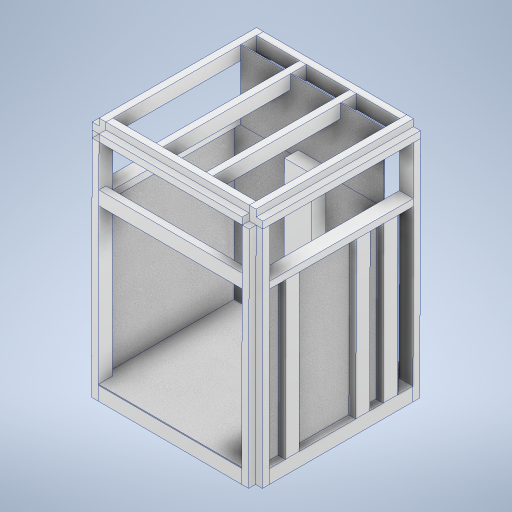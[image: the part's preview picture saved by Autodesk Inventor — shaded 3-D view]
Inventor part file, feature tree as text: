
AUTODESK INVENTOR PART (.ipt)
format: ipt  version: 2024 (Build 280153000, 153)  size: 792,576 bytes
history: native  units: mm
features: projected_geometry x19, extrude x18, sketch x17, mirror x2
ambient origin geometry x8: Origin, YZ Plane, XZ Plane, XY Plane, X Axis, Y Axis, Z Axis, Center Point
bodies: Solid1 (feature_tree), Solid2 (feature_tree), Solid3 (feature_tree), Solid4 (feature_tree), Solid5 (feature_tree), Solid6 (feature_tree), Solid7 (feature_tree), Solid8 (feature_tree), Solid12 (feature_tree), Solid16 (feature_tree), Solid17 (feature_tree), Solid18 (feature_tree), Solid19 (feature_tree), Solid20 (feature_tree), Solid22 (feature_tree), Solid23 (feature_tree), Solid24 (feature_tree), Solid25 (feature_tree)
feature tree (56):
  extrude  "Extrusion1"  Depth=495.0mm
  extrude  "Extrusion2"  Depth=40.0mm
  extrude  "Extrusion3"  Depth=20.0mm
  extrude  "Extrusion4"  Depth=40.0mm
  extrude  "Extrusion5"  Depth=20.0mm
  extrude  "Extrusion6"  Depth=40.0mm
  mirror  "Mirror1"
  extrude  "Extrusion7"  Depth=20.0mm
  extrude  "Extrusion8"  Depth=40.0mm
  extrude  "Extrusion12"  Depth=20.0mm
  mirror  "Mirror2"
  extrude  "Extrusion16"  Depth=40.0mm
  extrude  "Extrusion17"  Depth=20.0mm
  extrude  "Extrusion18"  Depth=40.0mm
  extrude  "Extrusion19"  Depth=20.0mm
  sketch  "Sketch23"  dims[d32=20.0mm d33=20.0mm]
  extrude  "Extrusion23"  Depth=20.0mm TaperAngle=0.0deg
  extrude  "Extrusion24"  Depth=40.0mm
  extrude  "Extrusion25"  Depth=20.0mm
  extrude  "Extrusion20"  Depth=40.0mm
  extrude  "Extrusion22"  Depth=20.0mm
  sketch  "Sketch1"  dims[d0=495.0mm d1=495.0mm]
  sketch  "Sketch2"  dims[d2=40.0mm d3=40.0mm]
  projected_geometry  "Projected Loop1"
  sketch  "Sketch3"  dims[d4=20.0mm d5=20.0mm]
  projected_geometry  "Projected Loop2"
  sketch  "Sketch4"  dims[d6=40.0mm d7=40.0mm]
  projected_geometry  "Projected Loop3"
  projected_geometry  "Projected Loop4"
  sketch  "Sketch5"  dims[d8=20.0mm d9=20.0mm]
  sketch  "Sketch6"  dims[d10=40.0mm d11=40.0mm]
  sketch  "Sketch7"  dims[d12=20.0mm d13=20.0mm]
  projected_geometry  "Projected Loop7"
  projected_geometry  "Projected Loop8"
  sketch  "Sketch8"  dims[d14=40.0mm d15=40.0mm]
  projected_geometry  "Projected Loop9"
  sketch  "Sketch12"  dims[d16=20.0mm d17=20.0mm]
  sketch  "Sketch16"  dims[d18=650.0mm d19=0.0mm d20=40.0mm]
  projected_geometry  "Projected Loop16"
  sketch  "Sketch17"  dims[d21=40.0mm d22=20.0mm]
  projected_geometry  "Projected Loop17"
  sketch  "Sketch18"  dims[d23=20.0mm d24=40.0mm]
  projected_geometry  "Projected Loop18"
  projected_geometry  "Projected Loop19"
  sketch  "Sketch19"  dims[d25=40.0mm d26=20.0mm]
  sketch  "Sketch20"  dims[d27=20.0mm d28=640.0mm d29=0.0mm]
  sketch  "Sketch22"  dims[d30=40.0mm d31=40.0mm]
  projected_geometry  "Projected Loop21"
  projected_geometry  "Projected Loop22"
  sketch  "Sketch24"  dims[d34=40.0mm d35=40.0mm d36=20.0mm d37=20.0mm d38=10.0mm d39=0.0mm d40=40.0mm d41=40.0mm d42=40.0mm d43=40.0mm d44=625.0mm d45=0.0mm d46=10.0mm d47=0.0mm d48=20.0mm d49=40.0mm d50=20.0mm d51=40.0mm d52=20.0mm d53=40.0mm d54=86.0mm d57=86.0mm d58=450.0mm d59=0.0mm d60=20.0mm d62=455.0mm d63=0.0mm d64=40.0mm d65=20.0mm d66=470.0mm d67=0.0mm d86=3.0mm d87=0.0mm d91=20.0mm d99=20.0mm d100=40.0mm d101=20.0mm d102=40.0mm d103=125.0mm d104=125.0mm d105=10.0mm d106=0.0mm d107=10.0mm d108=0.0mm d109=10.0mm d110=0.0mm d111=20.0mm d113=3.0mm d114=0.0mm d116=3.0mm d117=0.0mm d125=3.0mm d126=0.0mm d127=83.0mm d128=208.0mm d129=164.0mm d130=40.0mm d131=80.0mm d132=20.0mm d133=0.0mm d134=470.0mm d135=0.0mm d136=20.0mm d137=470.0mm d138=0.0mm d139=0.872665mm]
  projected_geometry  "Projected Loop23"
  projected_geometry  "Projected Loop24"
  projected_geometry  "Project Cut Edges1"
  projected_geometry  "Project Cut Edges2"
  projected_geometry  "Project Cut Edges3"
  projected_geometry  "Project Cut Edges4"
